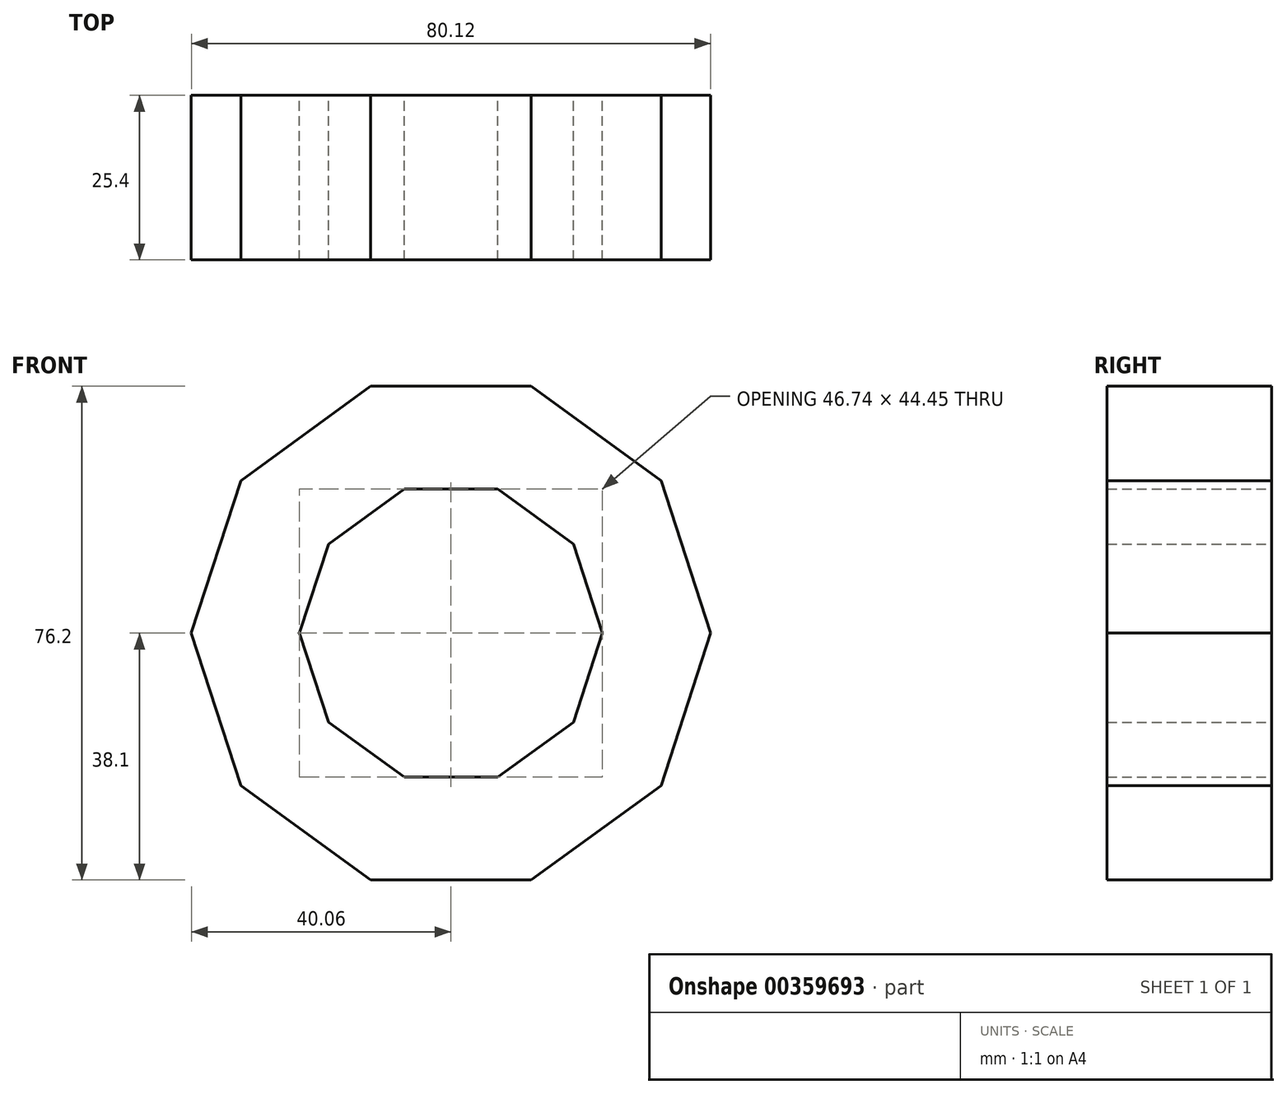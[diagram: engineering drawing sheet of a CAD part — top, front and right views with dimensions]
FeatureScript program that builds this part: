
annotation { "Feature Type Name" : "Feature", "Feature Type Description" : "" }
export const myFeature = defineFeature(function(context is Context, id is Id, definition is map)
    precondition{}
    {
        {
            var Q0;
            Q0=qCreatedBy(makeId("Front.planeOp"),FACE);
            var sketch = newSketch(context, id + "F0", { "sketchPlane" : qUnion([Q0])});
            skLineSegment(sketch, "E0", {"start": v(0, 0) * mm, "end": v(0, 38.1) * mm});
            skCircle(sketch, "E1.cCircle", {"center": v(0, 0) * mm, "radius": 38.1 * mm, "construction": true});
            skLineSegment(sketch, "E1.0", {"start": v(-12.38, 38.1) * mm, "end": v(12.38, 38.1) * mm});
            skLineSegment(sketch, "E1.1", {"start": v(12.38, 38.1) * mm, "end": v(32.4, 23.55) * mm});
            skLineSegment(sketch, "E1.2", {"start": v(32.4, 23.55) * mm, "end": v(40.06, 0) * mm});
            skLineSegment(sketch, "E1.3", {"start": v(40.06, 0) * mm, "end": v(32.4, -23.55) * mm});
            skLineSegment(sketch, "E1.4", {"start": v(32.4, -23.55) * mm, "end": v(12.38, -38.1) * mm});
            skLineSegment(sketch, "E1.5", {"start": v(12.38, -38.1) * mm, "end": v(-12.38, -38.1) * mm});
            skLineSegment(sketch, "E1.6", {"start": v(-12.38, -38.1) * mm, "end": v(-32.4, -23.55) * mm});
            skLineSegment(sketch, "E1.7", {"start": v(-32.4, -23.55) * mm, "end": v(-40.06, 0) * mm});
            skLineSegment(sketch, "E1.8", {"start": v(-40.06, 0) * mm, "end": v(-32.4, 23.55) * mm});
            skLineSegment(sketch, "E1.9", {"start": v(-32.4, 23.55) * mm, "end": v(-12.38, 38.1) * mm});
            skPoint(sketch, "E1.0.midPoint", {"position": v(0, 38.1) * mm});
            skPoint(sketch, "E2.0.midPoint", {"position": v(0, 25.4) * mm});
            skPoint(sketch, "E3.orphan", {"position": v(8.25, 25.4) * mm});
            skPoint(sketch, "E2.9.end.orphan", {"position": v(-8.25, 25.4) * mm});
            skLineSegment(sketch, "E4", {"start": v(0, 0) * mm, "end": v(0, 22.23) * mm});
            skCircle(sketch, "E5.cCircle", {"center": v(0, 0) * mm, "radius": 22.23 * mm, "construction": true});
            skLineSegment(sketch, "E5.0", {"start": v(-7.22, 22.23) * mm, "end": v(7.22, 22.23) * mm});
            skLineSegment(sketch, "E5.1", {"start": v(7.22, 22.23) * mm, "end": v(18.9, 13.74) * mm});
            skLineSegment(sketch, "E5.2", {"start": v(18.9, 13.74) * mm, "end": v(23.37, 0) * mm});
            skLineSegment(sketch, "E5.3", {"start": v(23.37, 0) * mm, "end": v(18.9, -13.74) * mm});
            skLineSegment(sketch, "E5.4", {"start": v(18.9, -13.74) * mm, "end": v(7.22, -22.23) * mm});
            skLineSegment(sketch, "E5.5", {"start": v(7.22, -22.23) * mm, "end": v(-7.22, -22.23) * mm});
            skLineSegment(sketch, "E5.6", {"start": v(-7.22, -22.23) * mm, "end": v(-18.9, -13.74) * mm});
            skLineSegment(sketch, "E5.7", {"start": v(-18.9, -13.74) * mm, "end": v(-23.37, 0) * mm});
            skLineSegment(sketch, "E5.8", {"start": v(-23.37, 0) * mm, "end": v(-18.9, 13.74) * mm});
            skLineSegment(sketch, "E5.9", {"start": v(-18.9, 13.74) * mm, "end": v(-7.22, 22.23) * mm});
            skPoint(sketch, "E5.0.midPoint", {"position": v(0, 22.23) * mm});
            skSolve(sketch);
        }
        {
            var Q0;
            {var subQ3=sQuery(id+"F0.wireOp",EDGE,"E1.1");Q0=makeQuery(id+"F0.imprint","IMPRINT",FACE,{"disambiguationData":[TD([[makeQuery(id+"F0.imprint","IMPRINT",EDGE,{"derivedFrom":subQ3}),-1.0]])]});}
            extrude(context, id + "F1", {"entities" : qUnion([Q0]), "depth" : 25.4 * mm});
        }
    });
